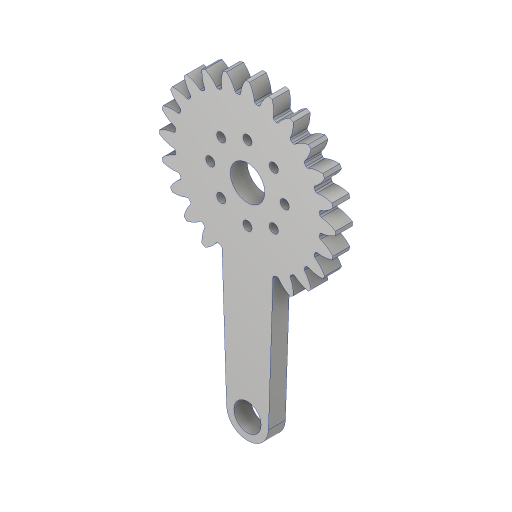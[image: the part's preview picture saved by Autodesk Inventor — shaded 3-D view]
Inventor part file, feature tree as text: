
AUTODESK INVENTOR PART (.ipt)
format: ipt  version: 2023.2 (Build 272271000, 271)  size: 366,080 bytes
history: native  units: mm
features: extrude x6, sketch x6, fillet x2, other x1, pattern_circular x1
ambient origin geometry x8: Origin, YZ Plane, XZ Plane, XY Plane, X Axis, Y Axis, Z Axis, Center Point
bodies: Body1 (feature_tree)
feature tree (16):
  other  "솔리드1"
  extrude  "돌출1"  Depth=48.0mm
  pattern_circular  "원형 패턴1"  [2 undecoded]
  extrude  "돌출2"  Depth=43.0mm
  extrude  "돌출3"  Depth=1.57mm
  extrude  "돌출4"  Depth=1.0mm
  fillet  "모깎기1"  Radius=0.5mm
  fillet  "모깎기2"  Radius=5.0mm
  extrude  "돌출5"  Depth=240.0mm TaperAngle=360.0deg
  extrude  "돌출6"  Depth=10.2mm
  sketch  "스케치1"
  sketch  "스케치2"
  sketch  "스케치3"
  sketch  "스케치4"
  sketch  "스케치5"
  sketch  "스케치6"
note: 2 required parameter values undecoded (feature->parameter linkage not recoverable at this tier; creation-order binding heuristic only, values carry confidence <= 0.55)
